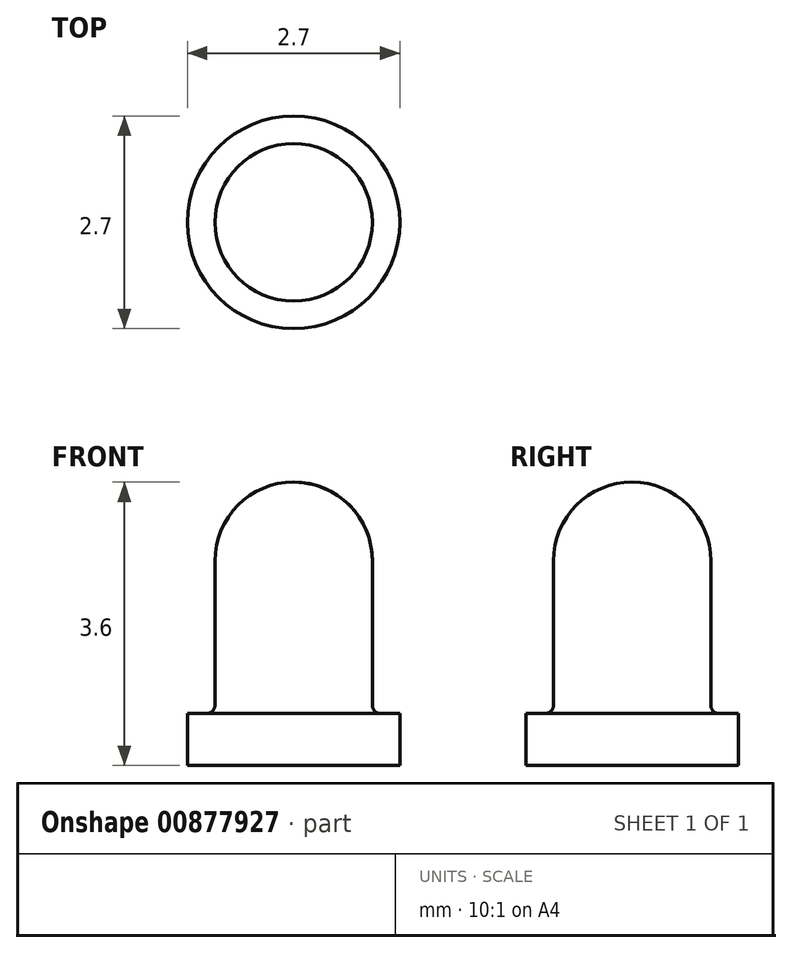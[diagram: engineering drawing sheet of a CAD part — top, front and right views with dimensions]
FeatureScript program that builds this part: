
annotation { "Feature Type Name" : "Feature", "Feature Type Description" : "" }
export const myFeature = defineFeature(function(context is Context, id is Id, definition is map)
    precondition{}
    {
        {
            var Q0;
            Q0=qCreatedBy(makeId("Front.planeOp"),FACE);
            var sketch = newSketch(context, id + "F0", { "sketchPlane" : qUnion([Q0])});
            skLineSegment(sketch, "E0.bottom", {"start": v(1, 1.5) * mm, "end": v(-1, 1.5) * mm});
            skLineSegment(sketch, "E0.top", {"start": v(1, -1.5) * mm, "end": v(-1, -1.5) * mm});
            skLineSegment(sketch, "E0.left", {"start": v(1, 1.5) * mm, "end": v(1, -1.5) * mm});
            skLineSegment(sketch, "E0.right", {"start": v(-1, 1.5) * mm, "end": v(-1, -1.5) * mm});
            skPoint(sketch, "E0.middle", {"position": v(0, 0) * mm});
            skCircle(sketch, "E1", {"center": v(0, 1.5) * mm, "radius": 1 * mm});
            skLineSegment(sketch, "E2.bottom", {"start": v(1.35, -1.1) * mm, "end": v(-1.35, -1.1) * mm});
            skLineSegment(sketch, "E2.top", {"start": v(1.35, -0.44) * mm, "end": v(-1.35, -0.44) * mm});
            skLineSegment(sketch, "E2.left", {"start": v(1.35, -1.1) * mm, "end": v(1.35, -0.44) * mm});
            skLineSegment(sketch, "E2.right", {"start": v(-1.35, -1.1) * mm, "end": v(-1.35, -0.44) * mm});
            skPoint(sketch, "E2.middle", {"position": v(0, -0.77) * mm});
            skLineSegment(sketch, "E3", {"start": v(0, -3.18) * mm, "end": v(0, 4.94) * mm});
            skSolve(sketch);
        }
        {
            var Q0;
            {var subQ0=sQuery(id+"F0.wireOp",EDGE,"E2.top");var subQ1=sQuery(id+"F0.wireOp",EDGE,"E0.left");var subQ2=makeQuery(id+"F0.imprint","INTERSECT",VERTEX,{"derivedFrom":[subQ1,subQ0]});Q0=makeQuery(id+"F0.imprint","IMPRINT",FACE,{"disambiguationData":[TD([[makeQuery(id+"F0.imprint","IMPRINT",EDGE,{"disambiguationData":[TD([[subQ2,-1.0]])],"derivedFrom":subQ1}),-1.0]])]});}
            var Q1;
            {var subQ1=sQuery(id+"F0.wireOp",EDGE,"E0.bottom");var subQ3=sQuery(id+"F0.wireOp",EDGE,"E3");var subQ4=makeQuery(id+"F0.imprint","INTERSECT",VERTEX,{"derivedFrom":[subQ1,subQ3]});Q1=makeQuery(id+"F0.imprint","IMPRINT",FACE,{"disambiguationData":[TD([[makeQuery(id+"F0.imprint","IMPRINT",EDGE,{"disambiguationData":[TD([[subQ4,1.0]])],"derivedFrom":subQ3}),-1.0]])]});}
            var Q2;
            {var subQ1=sQuery(id+"F0.wireOp",EDGE,"E0.left");var subQ3=sQuery(id+"F0.wireOp",EDGE,"E2.top");var subQ4=makeQuery(id+"F0.imprint","INTERSECT",VERTEX,{"derivedFrom":[subQ1,subQ3]});Q2=makeQuery(id+"F0.imprint","IMPRINT",FACE,{"disambiguationData":[TD([[makeQuery(id+"F0.imprint","IMPRINT",EDGE,{"disambiguationData":[TD([[subQ4,-1.0]])],"derivedFrom":subQ3}),-1.0]])]});}
            var Q3;
            {var subQ0=sQuery(id+"F0.wireOp",EDGE,"E1");var subQ3=sQuery(id+"F0.wireOp",EDGE,"E3");var subQ5=makeQuery(id+"F0.imprint","INTERSECT",VERTEX,{"disambiguationData":[OD(0.0)],"derivedFrom":[subQ0,subQ3]});Q3=makeQuery(id+"F0.imprint","IMPRINT",FACE,{"disambiguationData":[TD([[makeQuery(id+"F0.imprint","IMPRINT",EDGE,{"disambiguationData":[TD([[subQ5,1.0]])],"derivedFrom":subQ3}),-1.0]])]});}
            var Q4;
            {var subQ5=sQuery(id+"F0.wireOp",EDGE,"E2.left");Q4=makeQuery(id+"F0.imprint","IMPRINT",FACE,{"disambiguationData":[TD([[makeQuery(id+"F0.imprint","IMPRINT",EDGE,{"derivedFrom":subQ5}),1.0]])]});}
            var Q5;
            Q5=sQuery(id+"F0.wireOp",EDGE,"E3");
            revolve(context, id + "F1", {"surfaceOperationType" : NewSurfaceOperationType.NEW, "entities" : qUnion([Q0, Q1, Q2, Q3, Q4]), "axis" : qUnion([Q5]), "revolveType" : RevolveType.FULL});
        }
        {
            var Q0;
            Q0=makeQuery(id+"F1.opRevolve","SWEPT_EDGE",EDGE,{"disambiguationData":[OSD([sQuery(id+"F0.wireOp",EDGE,"E0.left"),sQuery(id+"F0.wireOp",EDGE,"E2.top")])]});
            fillet(context, id + "F2", {"entities" : qUnion([Q0]), "radius" : .1 * mm, "tangentPropagation" : true, "allowEdgeOverflow" : false});
        }
    });
